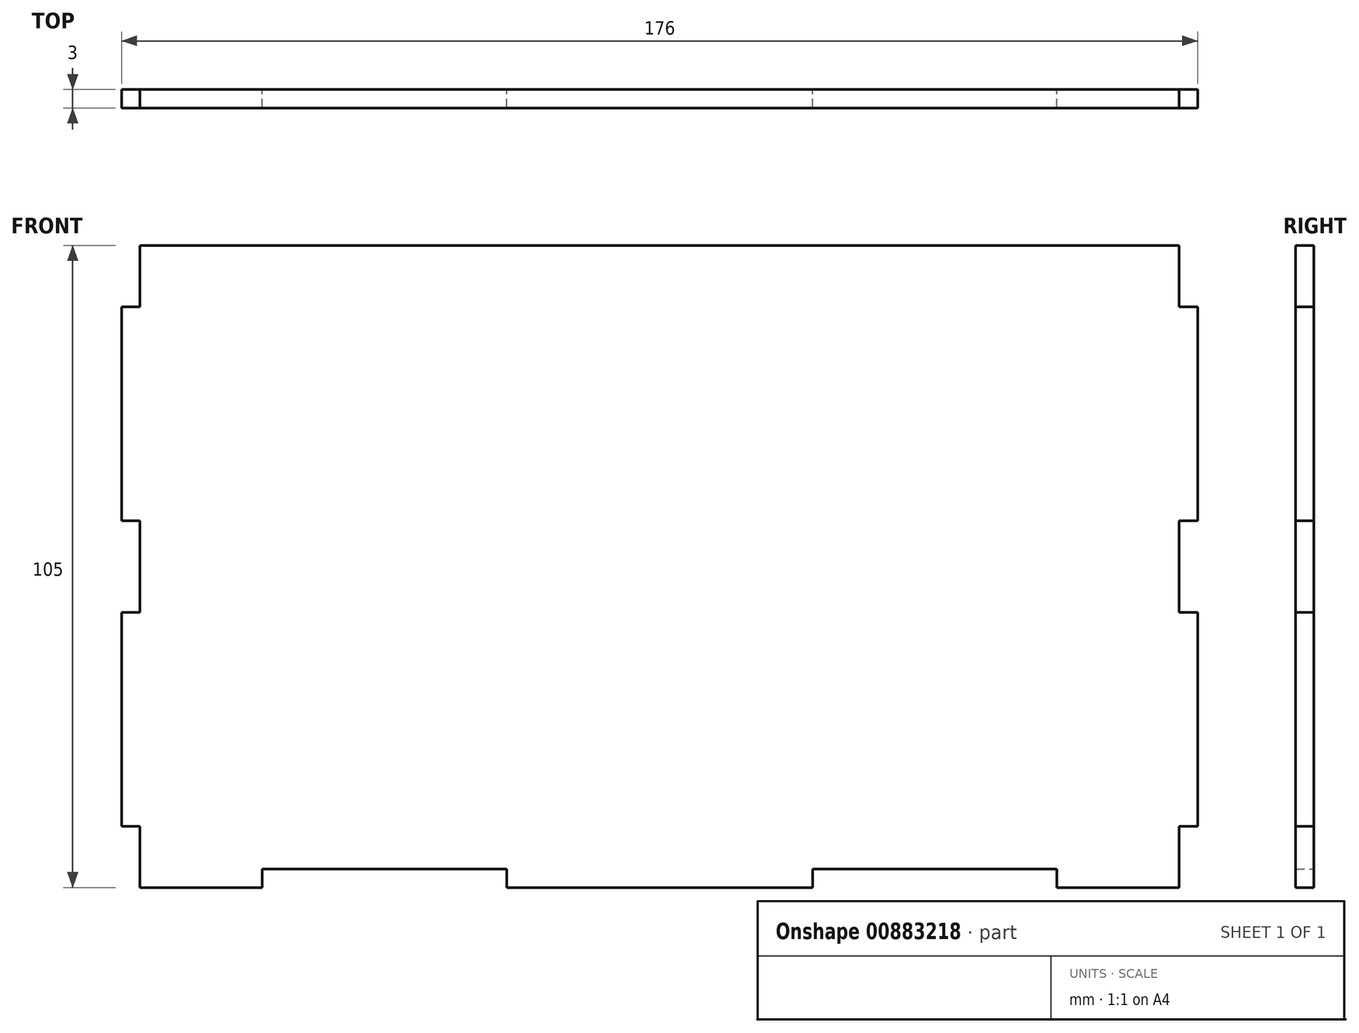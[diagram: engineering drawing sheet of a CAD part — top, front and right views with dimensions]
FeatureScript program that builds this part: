
annotation { "Feature Type Name" : "Feature", "Feature Type Description" : "" }
export const myFeature = defineFeature(function(context is Context, id is Id, definition is map)
    precondition{}
    {
        {
            var Q0;
            Q0=qCreatedBy(makeId("Front.planeOp"),FACE);
            var sketch = newSketch(context, id + "F0", { "sketchPlane" : qUnion([Q0])});
            skLineSegment(sketch, "E0.bottom", {"start": v(85, 52.5) * mm, "end": v(-85, 52.5) * mm});
            skLineSegment(sketch, "E0.top", {"start": v(85, -52.5) * mm, "end": v(-85, -52.5) * mm});
            skLineSegment(sketch, "E0.left", {"start": v(85, 52.5) * mm, "end": v(85, -52.5) * mm});
            skLineSegment(sketch, "E0.right", {"start": v(-85, 52.5) * mm, "end": v(-85, -52.5) * mm});
            skPoint(sketch, "E0.middle", {"position": v(0, 0) * mm});
            skLineSegment(sketch, "E1", {"start": v(25, -52.5) * mm, "end": v(25, -49.5) * mm});
            skLineSegment(sketch, "E2", {"start": v(25, -49.5) * mm, "end": v(65, -49.5) * mm});
            skLineSegment(sketch, "E3", {"start": v(65, -49.5) * mm, "end": v(65, -52.5) * mm});
            skLineSegment(sketch, "E4", {"start": v(85, -42.5) * mm, "end": v(88, -42.5) * mm});
            skLineSegment(sketch, "E5", {"start": v(88, -42.5) * mm, "end": v(88, -7.5) * mm});
            skLineSegment(sketch, "E6", {"start": v(88, -7.5) * mm, "end": v(85, -7.5) * mm});
            skLineSegment(sketch, "E7.MirrorCS", {"start": v(-85, -42.5) * mm, "end": v(-88, -42.5) * mm});
            skLineSegment(sketch, "E8.MirrorCS", {"start": v(-88, -42.5) * mm, "end": v(-88, -7.5) * mm});
            skLineSegment(sketch, "E9.MirrorCS", {"start": v(-88, -7.5) * mm, "end": v(-85, -7.5) * mm});
            skLineSegment(sketch, "E10", {"start": v(85, 42.5) * mm, "end": v(88, 42.5) * mm});
            skLineSegment(sketch, "E11", {"start": v(88, 42.5) * mm, "end": v(88, 7.5) * mm});
            skLineSegment(sketch, "E12", {"start": v(88, 7.5) * mm, "end": v(85, 7.5) * mm});
            skLineSegment(sketch, "E13.MirrorCS", {"start": v(-88, 7.5) * mm, "end": v(-85, 7.5) * mm});
            skLineSegment(sketch, "E14.MirrorCS", {"start": v(-88, 42.5) * mm, "end": v(-88, 7.5) * mm});
            skLineSegment(sketch, "E15.MirrorCS", {"start": v(-85, 42.5) * mm, "end": v(-88, 42.5) * mm});
            skLineSegment(sketch, "E16", {"start": v(-65, -52.5) * mm, "end": v(-65, -49.5) * mm});
            skLineSegment(sketch, "E17", {"start": v(-65, -49.5) * mm, "end": v(-25, -49.5) * mm});
            skLineSegment(sketch, "E18", {"start": v(-25, -49.5) * mm, "end": v(-25, -52.5) * mm});
            skSolve(sketch);
        }
        {
            var Q0;
            Q0=makeQuery(id+"F0.imprint","IMPRINT",FACE,{"disambiguationData":[TD([[makeQuery(id+"F0.imprint","IMPRINT",EDGE,{"derivedFrom":sQuery(id+"F0.wireOp",EDGE,"E0.bottom")}),1.0]])]});
            var Q1;
            {var subQ0=sQuery(id+"F0.wireOp",EDGE,"E7.MirrorCS");Q1=makeQuery(id+"F0.imprint","IMPRINT",FACE,{"disambiguationData":[TD([[makeQuery(id+"F0.imprint","IMPRINT",EDGE,{"derivedFrom":subQ0}),-1.0]])]});}
            var Q2;
            {var subQ0=sQuery(id+"F0.wireOp",EDGE,"E4");Q2=makeQuery(id+"F0.imprint","IMPRINT",FACE,{"disambiguationData":[TD([[makeQuery(id+"F0.imprint","IMPRINT",EDGE,{"derivedFrom":subQ0}),1.0]])]});}
            var Q3;
            {var subQ0=sQuery(id+"F0.wireOp",EDGE,"E10");Q3=makeQuery(id+"F0.imprint","IMPRINT",FACE,{"disambiguationData":[TD([[makeQuery(id+"F0.imprint","IMPRINT",EDGE,{"derivedFrom":subQ0}),-1.0]])]});}
            var Q4;
            {var subQ0=sQuery(id+"F0.wireOp",EDGE,"E13.MirrorCS");Q4=makeQuery(id+"F0.imprint","IMPRINT",FACE,{"disambiguationData":[TD([[makeQuery(id+"F0.imprint","IMPRINT",EDGE,{"derivedFrom":subQ0}),1.0]])]});}
            extrude(context, id + "F1", {"entities" : qUnion([Q0, Q1, Q2, Q3, Q4]), "depth" : 3 * mm, "offsetDistance" : 25 * mm});
        }
    });
